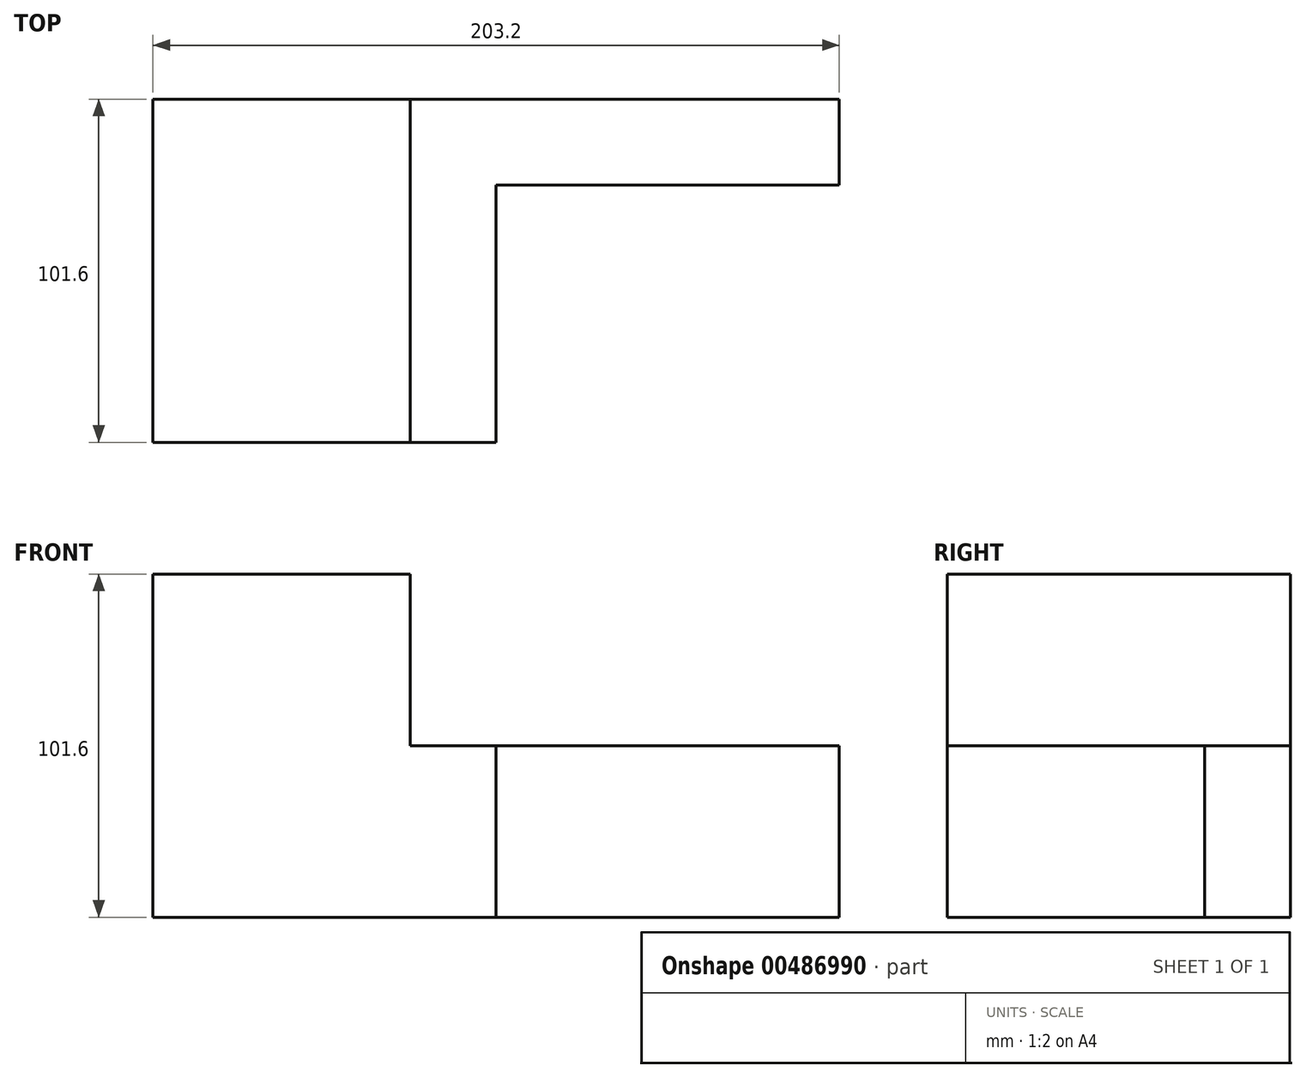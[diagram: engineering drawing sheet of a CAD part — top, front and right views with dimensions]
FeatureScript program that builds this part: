
annotation { "Feature Type Name" : "Feature", "Feature Type Description" : "" }
export const myFeature = defineFeature(function(context is Context, id is Id, definition is map)
    precondition{}
    {
        {
            var Q0;
            Q0=qCreatedBy(makeId("Front.planeOp"),FACE);
            var sketch = newSketch(context, id + "F0", { "sketchPlane" : qUnion([Q0])});
            skLineSegment(sketch, "E0.bottom", {"start": v(0, 0) * mm, "end": v(-76.2, 0) * mm});
            skLineSegment(sketch, "E0.top", {"start": v(0, 101.6) * mm, "end": v(-76.2, 101.6) * mm});
            skLineSegment(sketch, "E0.left", {"start": v(0, 0) * mm, "end": v(0, 101.6) * mm});
            skLineSegment(sketch, "E0.right", {"start": v(-76.2, 0) * mm, "end": v(-76.2, 101.6) * mm});
            skLineSegment(sketch, "E1.bottom", {"start": v(0, 0) * mm, "end": v(25.4, 0) * mm});
            skLineSegment(sketch, "E1.top", {"start": v(0, 50.8) * mm, "end": v(25.4, 50.8) * mm});
            skLineSegment(sketch, "E1.left", {"start": v(0, 0) * mm, "end": v(0, 50.8) * mm});
            skLineSegment(sketch, "E1.right", {"start": v(25.4, 0) * mm, "end": v(25.4, 50.8) * mm});
            skLineSegment(sketch, "E2.bottom", {"start": v(25.4, 0) * mm, "end": v(127, 0) * mm});
            skLineSegment(sketch, "E2.top", {"start": v(25.4, 50.8) * mm, "end": v(127, 50.8) * mm});
            skLineSegment(sketch, "E2.right", {"start": v(127, 0) * mm, "end": v(127, 50.8) * mm});
            skSolve(sketch);
        }
        {
            var Q0;
            Q0=makeQuery(id+"F0.imprint","IMPRINT",FACE,{"disambiguationData":[TD([[makeQuery(id+"F0.imprint","IMPRINT",EDGE,{"derivedFrom":sQuery(id+"F0.wireOp",EDGE,"E0.bottom")}),-1.0]])]});
            var Q1;
            Q1=makeQuery(id+"F0.imprint","IMPRINT",FACE,{"disambiguationData":[TD([[makeQuery(id+"F0.imprint","IMPRINT",EDGE,{"derivedFrom":sQuery(id+"F0.wireOp",EDGE,"E1.bottom")}),1.0]])]});
            extrude(context, id + "F1", {"entities" : qUnion([Q0, Q1]), "depth" : 101.6 * mm});
        }
        {
            var Q0;
            Q0=makeQuery(id+"F0.imprint","IMPRINT",FACE,{"disambiguationData":[TD([[makeQuery(id+"F0.imprint","IMPRINT",EDGE,{"derivedFrom":sQuery(id+"F0.wireOp",EDGE,"E2.bottom")}),1.0]])]});
            extrude(context, id + "F2", {"entities" : qUnion([Q0]), "operationType" : NewBodyOperationType.ADD, "depth" : 25.4 * mm});
        }
    });
